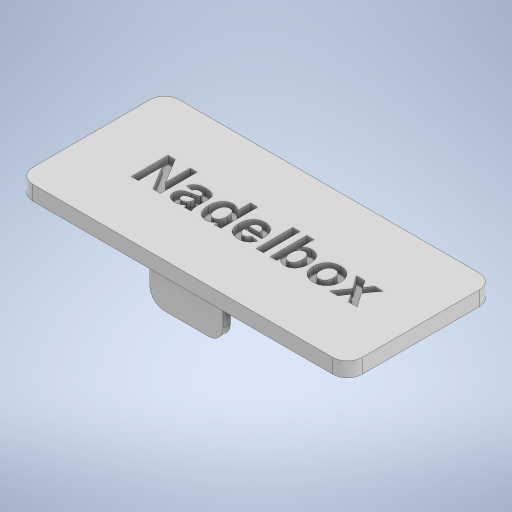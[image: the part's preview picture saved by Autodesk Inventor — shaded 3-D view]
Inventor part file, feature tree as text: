
AUTODESK INVENTOR PART (.ipt)
format: ipt  version: 2023.1 (Build 271208000, 208)  size: 451,584 bytes
history: native  units: mm
features: fillet x3, sketch x3, extrude x2, other x1
ambient origin geometry x8: Origin, YZ Plane, XZ Plane, XY Plane, X Axis, Y Axis, Z Axis, Center Point
bodies: Volumenkörper1 (feature_tree)
feature tree (9):
  extrude  "Extrusion1"  Depth=20.0mm
  extrude  "Extrusion2"  Depth=1.0mm
  fillet  "Rundung1"  Radius=2.0mm
  fillet  "Rundung2"  Radius=1.0mm
  fillet  "Rundung3"  Radius=1.0mm
  other  "Prägen1"
  sketch  "Skizze1"  dims[d0=45.0mm d1=20.0mm]
  sketch  "Skizze2"  dims[d2=10.0mm d3=22.5mm d4=2.0mm d5=0.0mm d6=1.0mm d7=1.0mm]
  sketch  "Skizze3"  dims[d8=0.5mm d9=10.0mm d10=10.0mm d11=0.5mm d12=5.0mm d13=4.5mm d14=0.0mm d15=2.0mm d16=2.0mm d17=2.0mm d18=1.0mm d19=0.0mm]
